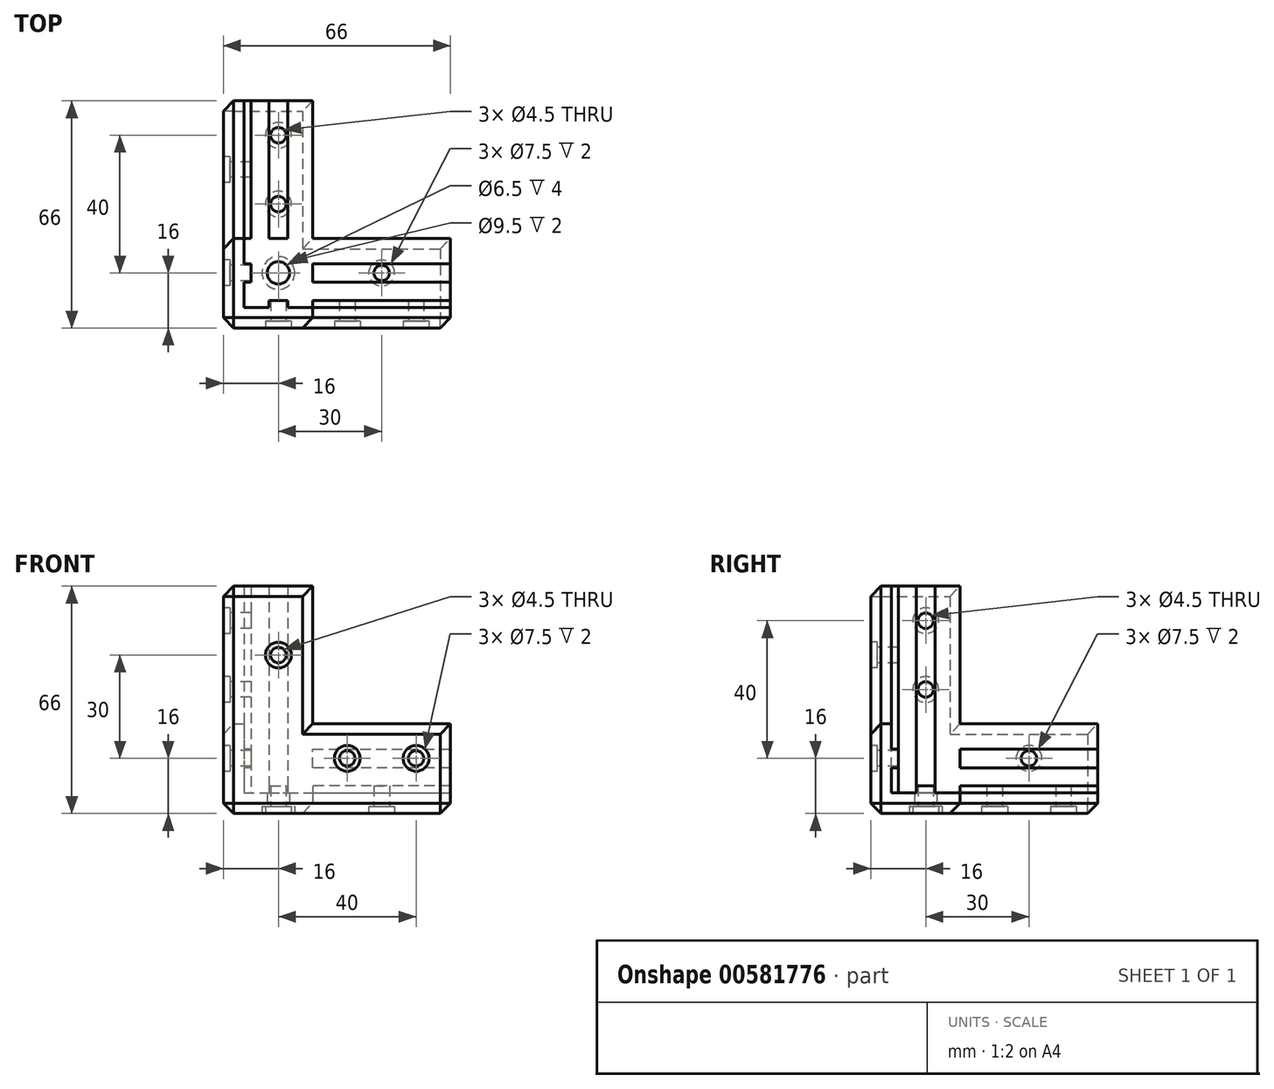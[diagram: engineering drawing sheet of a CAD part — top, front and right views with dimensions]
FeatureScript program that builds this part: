
annotation { "Feature Type Name" : "Feature", "Feature Type Description" : "" }
export const myFeature = defineFeature(function(context is Context, id is Id, definition is map)
    precondition{}
    {
        {
            var Q0;
            Q0=qCreatedBy(makeId("Top.planeOp"),FACE);
            var sketch = newSketch(context, id + "F0", { "sketchPlane" : qUnion([Q0])});
            skLineSegment(sketch, "E0", {"start": v(0, 0) * mm, "end": v(0, 66) * mm});
            skLineSegment(sketch, "E1", {"start": v(0, 66) * mm, "end": v(26, 66) * mm});
            skLineSegment(sketch, "E2", {"start": v(26, 66) * mm, "end": v(26, 26) * mm});
            skLineSegment(sketch, "E3", {"start": v(26, 26) * mm, "end": v(66, 26) * mm});
            skLineSegment(sketch, "E4", {"start": v(66, 26) * mm, "end": v(66, 0) * mm});
            skLineSegment(sketch, "E5", {"start": v(66, 0) * mm, "end": v(0, 0) * mm});
            skLineSegment(sketch, "E6", {"start": v(66, 6) * mm, "end": v(6, 6) * mm, "construction": true});
            skLineSegment(sketch, "E7", {"start": v(6, 6) * mm, "end": v(6, 66) * mm, "construction": true});
            skSolve(sketch);
        }
        {
            var Q0;
            Q0=qSketchRegion(id+"F0",true);
            extrude(context, id + "F1", {"entities" : qUnion([Q0]), "depth" : 6 * mm});
        }
        {
            var Q0;
            Q0=makeQuery(id+"F1.opExtrude","CAP_FACE",FACE,{"disambiguationData":[OSD([sQuery(id+"F0.wireOp",EDGE,"E0"),sQuery(id+"F0.wireOp",EDGE,"E1"),sQuery(id+"F0.wireOp",EDGE,"E2"),sQuery(id+"F0.wireOp",EDGE,"E3"),sQuery(id+"F0.wireOp",EDGE,"E4"),sQuery(id+"F0.wireOp",EDGE,"E5")])],"isStart":false});
            var sketch = newSketch(context, id + "F2", { "sketchPlane" : qUnion([Q0])});
            skLineSegment(sketch, "E8", {"start": v(0, 66) * mm, "end": v(6, 66) * mm});
            skLineSegment(sketch, "E9", {"start": v(6, 66) * mm, "end": v(6, 6) * mm});
            skLineSegment(sketch, "E10", {"start": v(6, 6) * mm, "end": v(66, 6) * mm});
            skLineSegment(sketch, "E11", {"start": v(66, 6) * mm, "end": v(66, 0) * mm});
            skLineSegment(sketch, "E12", {"start": v(66, 0) * mm, "end": v(0, 0) * mm});
            skLineSegment(sketch, "E13", {"start": v(0, 0) * mm, "end": v(0, 66) * mm});
            skSolve(sketch);
        }
        {
            var Q0;
            Q0=makeQuery(id+"F2.imprint","IMPRINT",FACE,{"disambiguationData":[TD([[makeQuery(id+"F2.imprint","IMPRINT",EDGE,{"derivedFrom":sQuery(id+"F2.wireOp",EDGE,"E8")}),-1.0]])]});
            extrude(context, id + "F3", {"entities" : qUnion([Q0]), "operationType" : NewBodyOperationType.ADD, "depth" : 20 * mm});
        }
        {
            var Q0;
            Q0=makeQuery(id+"F3.opExtrude","CAP_FACE",FACE,{"disambiguationData":[OSD([sQuery(id+"F2.wireOp",EDGE,"E8"),sQuery(id+"F2.wireOp",EDGE,"E9"),sQuery(id+"F2.wireOp",EDGE,"E10"),sQuery(id+"F2.wireOp",EDGE,"E11"),sQuery(id+"F2.wireOp",EDGE,"E12"),sQuery(id+"F2.wireOp",EDGE,"E13")])],"isStart":false});
            var sketch = newSketch(context, id + "F4", { "sketchPlane" : qUnion([Q0])});
            skLineSegment(sketch, "E14", {"start": v(6, 26) * mm, "end": v(0, 26) * mm});
            skLineSegment(sketch, "E15", {"start": v(0, 26) * mm, "end": v(0, 0) * mm});
            skLineSegment(sketch, "E16", {"start": v(0, 0) * mm, "end": v(26, 0) * mm});
            skLineSegment(sketch, "E17", {"start": v(26, 0) * mm, "end": v(26, 6) * mm});
            skLineSegment(sketch, "E18", {"start": v(26, 6) * mm, "end": v(6, 6) * mm});
            skLineSegment(sketch, "E19", {"start": v(6, 6) * mm, "end": v(6, 26) * mm});
            skSolve(sketch);
        }
        {
            var Q0;
            Q0=qSketchRegion(id+"F4",true);
            extrude(context, id + "F5", {"entities" : qUnion([Q0]), "operationType" : NewBodyOperationType.ADD, "depth" : 40 * mm});
        }
        {
            var Q0;
            Q0=makeQuery(id+"F1.opExtrude","CAP_FACE",FACE,{"disambiguationData":[OSD([sQuery(id+"F0.wireOp",EDGE,"E0"),sQuery(id+"F0.wireOp",EDGE,"E1"),sQuery(id+"F0.wireOp",EDGE,"E2"),sQuery(id+"F0.wireOp",EDGE,"E3"),sQuery(id+"F0.wireOp",EDGE,"E4"),sQuery(id+"F0.wireOp",EDGE,"E5")])],"isStart":false});
            var sketch = newSketch(context, id + "F6", { "sketchPlane" : qUnion([Q0])});
            skLineSegment(sketch, "E20", {"start": v(66, 16) * mm, "end": v(6, 16) * mm, "construction": true});
            skLineSegment(sketch, "E21", {"start": v(16, 66) * mm, "end": v(16, 6) * mm, "construction": true});
            skLineSegment(sketch, "E22", {"start": v(16, 6) * mm, "end": v(18.71, 6) * mm});
            skLineSegment(sketch, "E23", {"start": v(18.71, 6) * mm, "end": v(18.71, 8) * mm});
            skLineSegment(sketch, "E24", {"start": v(18.71, 8) * mm, "end": v(13.3, 8) * mm});
            skLineSegment(sketch, "E25", {"start": v(13.3, 8) * mm, "end": v(13.3, 6) * mm});
            skLineSegment(sketch, "E26", {"start": v(13.3, 6) * mm, "end": v(16, 6) * mm});
            skLineSegment(sketch, "E27", {"start": v(6, 16) * mm, "end": v(6, 18.7) * mm});
            skLineSegment(sketch, "E28", {"start": v(6, 18.7) * mm, "end": v(8, 18.7) * mm});
            skLineSegment(sketch, "E29", {"start": v(8, 18.7) * mm, "end": v(8, 13.29) * mm});
            skLineSegment(sketch, "E30", {"start": v(8, 13.29) * mm, "end": v(6, 13.29) * mm});
            skLineSegment(sketch, "E31", {"start": v(6, 13.29) * mm, "end": v(6, 16) * mm});
            skSolve(sketch);
        }
        {
            var Q0;
            Q0=qSketchRegion(id+"F6",true);
            extrude(context, id + "F7", {"entities" : qUnion([Q0]), "operationType" : NewBodyOperationType.ADD, "depth" : 60 * mm});
        }
        {
            var Q0;
            Q0=makeQuery(id+"F1.opExtrude","CAP_FACE",FACE,{"disambiguationData":[OSD([sQuery(id+"F0.wireOp",EDGE,"E0"),sQuery(id+"F0.wireOp",EDGE,"E1"),sQuery(id+"F0.wireOp",EDGE,"E2"),sQuery(id+"F0.wireOp",EDGE,"E3"),sQuery(id+"F0.wireOp",EDGE,"E4"),sQuery(id+"F0.wireOp",EDGE,"E5")])],"isStart":false});
            var sketch = newSketch(context, id + "F8", { "sketchPlane" : qUnion([Q0])});
            skLineSegment(sketch, "E32", {"start": v(66, 16) * mm, "end": v(8, 16) * mm, "construction": true});
            skLineSegment(sketch, "E33", {"start": v(66, 16) * mm, "end": v(66, 18.7) * mm});
            skLineSegment(sketch, "E34", {"start": v(66, 18.7) * mm, "end": v(26, 18.7) * mm});
            skLineSegment(sketch, "E35", {"start": v(26, 18.7) * mm, "end": v(26, 13.29) * mm});
            skLineSegment(sketch, "E36", {"start": v(26, 13.29) * mm, "end": v(66, 13.29) * mm});
            skLineSegment(sketch, "E37", {"start": v(66, 13.29) * mm, "end": v(66, 16) * mm});
            skLineSegment(sketch, "E38", {"start": v(16, 66) * mm, "end": v(16, 8) * mm, "construction": true});
            skLineSegment(sketch, "E39", {"start": v(16, 66) * mm, "end": v(13.3, 66) * mm});
            skLineSegment(sketch, "E40", {"start": v(13.3, 66) * mm, "end": v(13.3, 26) * mm});
            skLineSegment(sketch, "E41", {"start": v(13.3, 26) * mm, "end": v(18.7, 26) * mm});
            skLineSegment(sketch, "E42", {"start": v(18.7, 26) * mm, "end": v(18.7, 66) * mm});
            skLineSegment(sketch, "E43", {"start": v(18.7, 66) * mm, "end": v(16, 66) * mm});
            skSolve(sketch);
        }
        {
            var Q0;
            Q0=qSketchRegion(id+"F8",true);
            extrude(context, id + "F9", {"entities" : qUnion([Q0]), "operationType" : NewBodyOperationType.ADD, "depth" : 2 * mm});
        }
        {
            var Q0;
            {var subQ1=sQuery(id+"F2.wireOp",EDGE,"E10");var subQ2=sQuery(id+"F0.wireOp",EDGE,"E4");var subQ3=sQuery(id+"F4.wireOp",EDGE,"E18");Q0=makeQuery(id+"F7.boolean.opBoolean","SPLIT",FACE,{"disambiguationData":[TD([makeQuery(id+"F1.opExtrude","SWEPT_FACE",FACE,{"disambiguationData":[OSD([subQ2])]})])],"derivedFrom":makeQuery(id+"F5.boolean.opBoolean","MERGE",FACE,{"derivedFrom":[makeQuery(id+"F3.opExtrude","SWEPT_FACE",FACE,{"disambiguationData":[OSD([subQ1])]}),makeQuery(id+"F5.opExtrude","SWEPT_FACE",FACE,{"disambiguationData":[OSD([subQ3])]})]})});}
            var sketch = newSketch(context, id + "F10", { "sketchPlane" : qUnion([Q0])});
            skLineSegment(sketch, "E44", {"start": v(-66, 16) * mm, "end": v(-26, 16) * mm, "construction": true});
            skLineSegment(sketch, "E45", {"start": v(-66, 16) * mm, "end": v(-66, 13.3) * mm});
            skLineSegment(sketch, "E46", {"start": v(-66, 13.3) * mm, "end": v(-26, 13.3) * mm});
            skLineSegment(sketch, "E47", {"start": v(-26, 13.3) * mm, "end": v(-26, 16) * mm});
            skLineSegment(sketch, "E48", {"start": v(-26, 18.71) * mm, "end": v(-66, 18.71) * mm});
            skLineSegment(sketch, "E49", {"start": v(-66, 18.71) * mm, "end": v(-66, 16) * mm});
            skLineSegment(sketch, "E50", {"start": v(-26, 18.71) * mm, "end": v(-26, 16) * mm});
            skSolve(sketch);
        }
        {
            var Q0;
            Q0=qSketchRegion(id+"F10",true);
            extrude(context, id + "F11", {"entities" : qUnion([Q0]), "operationType" : NewBodyOperationType.ADD, "depth" : 2 * mm});
        }
        {
            var Q0;
            {var subQ0=sQuery(id+"F2.wireOp",EDGE,"E9");var subQ3=sQuery(id+"F0.wireOp",EDGE,"E1");var subQ5=sQuery(id+"F4.wireOp",EDGE,"E19");Q0=makeQuery(id+"F7.boolean.opBoolean","SPLIT",FACE,{"disambiguationData":[TD([makeQuery(id+"F1.opExtrude","SWEPT_FACE",FACE,{"disambiguationData":[OSD([subQ3])]})])],"derivedFrom":makeQuery(id+"F5.boolean.opBoolean","MERGE",FACE,{"derivedFrom":[makeQuery(id+"F3.opExtrude","SWEPT_FACE",FACE,{"disambiguationData":[OSD([subQ0])]}),makeQuery(id+"F5.opExtrude","SWEPT_FACE",FACE,{"disambiguationData":[OSD([subQ5])]})]})});}
            var sketch = newSketch(context, id + "F12", { "sketchPlane" : qUnion([Q0])});
            skLineSegment(sketch, "E51", {"start": v(66, 16) * mm, "end": v(26, 16) * mm, "construction": true});
            skLineSegment(sketch, "E52", {"start": v(66, 16) * mm, "end": v(66, 18.71) * mm});
            skLineSegment(sketch, "E53", {"start": v(66, 18.71) * mm, "end": v(26, 18.7) * mm});
            skLineSegment(sketch, "E54", {"start": v(26, 18.7) * mm, "end": v(26, 13.29) * mm});
            skLineSegment(sketch, "E55", {"start": v(26, 13.29) * mm, "end": v(66, 13.29) * mm});
            skLineSegment(sketch, "E56", {"start": v(66, 16) * mm, "end": v(66, 13.29) * mm});
            skSolve(sketch);
        }
        {
            var Q0;
            Q0=qSketchRegion(id+"F12",true);
            extrude(context, id + "F13", {"entities" : qUnion([Q0]), "operationType" : NewBodyOperationType.ADD, "depth" : 2 * mm});
        }
        {
            var Q0;
            Q0=makeQuery(id+"F5.boolean.opBoolean","MERGE",FACE,{"derivedFrom":[makeQuery(id+"F3.boolean.opBoolean","MERGE",FACE,{"derivedFrom":[makeQuery(id+"F1.opExtrude","SWEPT_FACE",FACE,{"disambiguationData":[OSD([sQuery(id+"F0.wireOp",EDGE,"E5")])]}),makeQuery(id+"F3.opExtrude","SWEPT_FACE",FACE,{"disambiguationData":[OSD([sQuery(id+"F2.wireOp",EDGE,"E12")])]})]}),makeQuery(id+"F5.opExtrude","SWEPT_FACE",FACE,{"disambiguationData":[OSD([sQuery(id+"F4.wireOp",EDGE,"E16")])]})]});
            var sketch = newSketch(context, id + "F14", { "sketchPlane" : qUnion([Q0])});
            skLineSegment(sketch, "E57", {"start": v(6, 66) * mm, "end": v(6, 6) * mm, "construction": true});
            skLineSegment(sketch, "E58", {"start": v(6, 6) * mm, "end": v(66, 6) * mm, "construction": true});
            skCircle(sketch, "E59", {"center": v(56, 16) * mm, "radius": 2.25 * mm});
            skCircle(sketch, "E60", {"center": v(36, 16) * mm, "radius": 2.25 * mm});
            skCircle(sketch, "E61", {"center": v(16, 46) * mm, "radius": 2.25 * mm});
            skLineSegment(sketch, "E62", {"start": v(26, 26) * mm, "end": v(6, 26) * mm, "construction": true});
            skLineSegment(sketch, "E63", {"start": v(26, 26) * mm, "end": v(26, 6) * mm, "construction": true});
            skSolve(sketch);
        }
        {
            var Q0;
            Q0=makeQuery(id+"F14.imprint","IMPRINT",FACE,{"disambiguationData":[TD([[makeQuery(id+"F14.imprint","IMPRINT",EDGE,{"derivedFrom":sQuery(id+"F14.wireOp",EDGE,"E59")}),1.0]])]});
            var Q1;
            Q1=makeQuery(id+"F14.imprint","IMPRINT",FACE,{"disambiguationData":[TD([[makeQuery(id+"F14.imprint","IMPRINT",EDGE,{"derivedFrom":sQuery(id+"F14.wireOp",EDGE,"E61")}),1.0]])]});
            var Q2;
            Q2=makeQuery(id+"F14.imprint","IMPRINT",FACE,{"disambiguationData":[TD([[makeQuery(id+"F14.imprint","IMPRINT",EDGE,{"derivedFrom":sQuery(id+"F14.wireOp",EDGE,"E60")}),1.0]])]});
            extrude(context, id + "F15", {"entities" : qUnion([Q0, Q1, Q2]), "operationType" : NewBodyOperationType.REMOVE, "endBound" : BoundingType.UP_TO_NEXT, "oppositeDirection" : true, "depth" : 25 * mm});
        }
        {
            var Q0;
            Q0=makeQuery(id+"F5.boolean.opBoolean","MERGE",FACE,{"derivedFrom":[makeQuery(id+"F3.boolean.opBoolean","MERGE",FACE,{"derivedFrom":[makeQuery(id+"F1.opExtrude","SWEPT_FACE",FACE,{"disambiguationData":[OSD([sQuery(id+"F0.wireOp",EDGE,"E0")])]}),makeQuery(id+"F3.opExtrude","SWEPT_FACE",FACE,{"disambiguationData":[OSD([sQuery(id+"F2.wireOp",EDGE,"E13")])]})]}),makeQuery(id+"F5.opExtrude","SWEPT_FACE",FACE,{"disambiguationData":[OSD([sQuery(id+"F4.wireOp",EDGE,"E15")])]})]});
            var sketch = newSketch(context, id + "F16", { "sketchPlane" : qUnion([Q0])});
            skLineSegment(sketch, "E64", {"start": v(-6, 66) * mm, "end": v(-6, 6) * mm, "construction": true});
            skLineSegment(sketch, "E65", {"start": v(-6, 6) * mm, "end": v(-66, 6) * mm, "construction": true});
            skCircle(sketch, "E66", {"center": v(-16, 56) * mm, "radius": 2.25 * mm});
            skCircle(sketch, "E67", {"center": v(-46, 16) * mm, "radius": 2.25 * mm});
            skCircle(sketch, "E68", {"center": v(-16, 36) * mm, "radius": 2.25 * mm});
            skSolve(sketch);
        }
        {
            var Q0;
            Q0=qSketchRegion(id+"F16",true);
            extrude(context, id + "F17", {"entities" : qUnion([Q0]), "operationType" : NewBodyOperationType.REMOVE, "endBound" : BoundingType.UP_TO_NEXT, "oppositeDirection" : true, "depth" : 25 * mm});
        }
        {
            var Q0;
            Q0=makeQuery(id+"F1.opExtrude","CAP_FACE",FACE,{"disambiguationData":[OSD([sQuery(id+"F0.wireOp",EDGE,"E0"),sQuery(id+"F0.wireOp",EDGE,"E1"),sQuery(id+"F0.wireOp",EDGE,"E2"),sQuery(id+"F0.wireOp",EDGE,"E3"),sQuery(id+"F0.wireOp",EDGE,"E4"),sQuery(id+"F0.wireOp",EDGE,"E5")])],"isStart":true});
            var sketch = newSketch(context, id + "F18", { "sketchPlane" : qUnion([Q0])});
            skLineSegment(sketch, "E69", {"start": v(66, -6) * mm, "end": v(6, -6) * mm, "construction": true});
            skLineSegment(sketch, "E70", {"start": v(6, -6) * mm, "end": v(6, -66) * mm, "construction": true});
            skCircle(sketch, "E71", {"center": v(16, -16) * mm, "radius": 3.25 * mm});
            skCircle(sketch, "E72", {"center": v(46, -16) * mm, "radius": 2.25 * mm});
            skCircle(sketch, "E73", {"center": v(16, -56) * mm, "radius": 2.25 * mm});
            skCircle(sketch, "E74", {"center": v(16, -36) * mm, "radius": 2.25 * mm});
            skSolve(sketch);
        }
        {
            var Q0;
            Q0=qSketchRegion(id+"F18",true);
            extrude(context, id + "F19", {"entities" : qUnion([Q0]), "operationType" : NewBodyOperationType.REMOVE, "endBound" : BoundingType.UP_TO_NEXT, "oppositeDirection" : true, "depth" : 25 * mm});
        }
        {
            var Q0;
            Q0=makeQuery(id+"F5.boolean.opBoolean","MERGE",FACE,{"derivedFrom":[makeQuery(id+"F3.boolean.opBoolean","MERGE",FACE,{"derivedFrom":[makeQuery(id+"F1.opExtrude","SWEPT_FACE",FACE,{"disambiguationData":[OSD([sQuery(id+"F0.wireOp",EDGE,"E5")])]}),makeQuery(id+"F3.opExtrude","SWEPT_FACE",FACE,{"disambiguationData":[OSD([sQuery(id+"F2.wireOp",EDGE,"E12")])]})]}),makeQuery(id+"F5.opExtrude","SWEPT_FACE",FACE,{"disambiguationData":[OSD([sQuery(id+"F4.wireOp",EDGE,"E16")])]})]});
            var sketch = newSketch(context, id + "F20", { "sketchPlane" : qUnion([Q0])});
            skCircle(sketch, "E75", {"center": v(16, 46) * mm, "radius": 3.75 * mm});
            skCircle(sketch, "E76", {"center": v(36, 16) * mm, "radius": 3.75 * mm});
            skCircle(sketch, "E77", {"center": v(56, 16) * mm, "radius": 3.75 * mm});
            skSolve(sketch);
        }
        {
            var Q0;
            Q0=qSketchRegion(id+"F20",true);
            extrude(context, id + "F21", {"entities" : qUnion([Q0]), "operationType" : NewBodyOperationType.REMOVE, "oppositeDirection" : true, "depth" : 2 * mm});
        }
        {
            var Q0;
            Q0=makeQuery(id+"F5.boolean.opBoolean","MERGE",FACE,{"derivedFrom":[makeQuery(id+"F3.boolean.opBoolean","MERGE",FACE,{"derivedFrom":[makeQuery(id+"F1.opExtrude","SWEPT_FACE",FACE,{"disambiguationData":[OSD([sQuery(id+"F0.wireOp",EDGE,"E0")])]}),makeQuery(id+"F3.opExtrude","SWEPT_FACE",FACE,{"disambiguationData":[OSD([sQuery(id+"F2.wireOp",EDGE,"E13")])]})]}),makeQuery(id+"F5.opExtrude","SWEPT_FACE",FACE,{"disambiguationData":[OSD([sQuery(id+"F4.wireOp",EDGE,"E15")])]})]});
            var sketch = newSketch(context, id + "F22", { "sketchPlane" : qUnion([Q0])});
            skCircle(sketch, "E78", {"center": v(-16, 56) * mm, "radius": 3.75 * mm});
            skCircle(sketch, "E79", {"center": v(-46, 16) * mm, "radius": 3.75 * mm});
            skCircle(sketch, "E80", {"center": v(-16, 36) * mm, "radius": 3.75 * mm});
            skSolve(sketch);
        }
        {
            var Q0;
            Q0=qSketchRegion(id+"F22",true);
            extrude(context, id + "F23", {"entities" : qUnion([Q0]), "operationType" : NewBodyOperationType.REMOVE, "oppositeDirection" : true, "depth" : 2 * mm});
        }
        {
            var Q0;
            Q0=makeQuery(id+"F1.opExtrude","CAP_FACE",FACE,{"disambiguationData":[OSD([sQuery(id+"F0.wireOp",EDGE,"E0"),sQuery(id+"F0.wireOp",EDGE,"E1"),sQuery(id+"F0.wireOp",EDGE,"E2"),sQuery(id+"F0.wireOp",EDGE,"E3"),sQuery(id+"F0.wireOp",EDGE,"E4"),sQuery(id+"F0.wireOp",EDGE,"E5")])],"isStart":true});
            var sketch = newSketch(context, id + "F24", { "sketchPlane" : qUnion([Q0])});
            skCircle(sketch, "E81", {"center": v(16, -56) * mm, "radius": 3.75 * mm});
            skCircle(sketch, "E82", {"center": v(16, -16) * mm, "radius": 4.75 * mm});
            skCircle(sketch, "E83", {"center": v(46, -16) * mm, "radius": 3.75 * mm});
            skCircle(sketch, "E84", {"center": v(16, -36) * mm, "radius": 3.75 * mm});
            skSolve(sketch);
        }
        {
            var Q0;
            Q0=qSketchRegion(id+"F24",true);
            extrude(context, id + "F25", {"entities" : qUnion([Q0]), "operationType" : NewBodyOperationType.REMOVE, "oppositeDirection" : true, "depth" : 2 * mm});
        }
        {
            var Q0;
            Q0=makeQuery(id+"F1.opExtrude","CAP_EDGE",EDGE,{"disambiguationData":[OSD([sQuery(id+"F0.wireOp",EDGE,"E5")])],"isStart":true});
            var Q1;
            Q1=makeQuery(id+"F1.opExtrude","CAP_EDGE",EDGE,{"disambiguationData":[OSD([sQuery(id+"F0.wireOp",EDGE,"E0")])],"isStart":true});
            var Q2;
            Q2=makeQuery(id+"F5.boolean.opBoolean","MERGE",EDGE,{"derivedFrom":[makeQuery(id+"F3.boolean.opBoolean","MERGE",EDGE,{"derivedFrom":[makeQuery(id+"F1.opExtrude","SWEPT_EDGE",EDGE,{"disambiguationData":[OSD([sQuery(id+"F0.wireOp",EDGE,"E0"),sQuery(id+"F0.wireOp",EDGE,"E5")])]}),makeQuery(id+"F3.opExtrude","SWEPT_EDGE",EDGE,{"disambiguationData":[OSD([sQuery(id+"F2.wireOp",EDGE,"E12"),sQuery(id+"F2.wireOp",EDGE,"E13")])]})]}),makeQuery(id+"F5.opExtrude","SWEPT_EDGE",EDGE,{"disambiguationData":[OSD([sQuery(id+"F4.wireOp",EDGE,"E15"),sQuery(id+"F4.wireOp",EDGE,"E16")])]})]});
            var Q3;
            Q3=makeQuery(id+"F5.opExtrude","SWEPT_EDGE",EDGE,{"disambiguationData":[OSD([sQuery(id+"F2.wireOp",EDGE,"E13"),sQuery(id+"F4.wireOp",EDGE,"E14"),sQuery(id+"F4.wireOp",EDGE,"E15")])]});
            var Q4;
            Q4=makeQuery(id+"F3.opExtrude","CAP_EDGE",EDGE,{"disambiguationData":[OSD([sQuery(id+"F2.wireOp",EDGE,"E13")])],"isStart":false});
            var Q5;
            Q5=makeQuery(id+"F5.opExtrude","SWEPT_EDGE",EDGE,{"disambiguationData":[OSD([sQuery(id+"F2.wireOp",EDGE,"E12"),sQuery(id+"F4.wireOp",EDGE,"E16"),sQuery(id+"F4.wireOp",EDGE,"E17")])]});
            var Q6;
            Q6=makeQuery(id+"F3.opExtrude","CAP_EDGE",EDGE,{"disambiguationData":[OSD([sQuery(id+"F2.wireOp",EDGE,"E12")])],"isStart":false});
            var Q7;
            Q7=makeQuery(id+"F5.opExtrude","CAP_EDGE",EDGE,{"disambiguationData":[OSD([sQuery(id+"F4.wireOp",EDGE,"E15")])],"isStart":false});
            var Q8;
            Q8=makeQuery(id+"F5.opExtrude","CAP_EDGE",EDGE,{"disambiguationData":[OSD([sQuery(id+"F4.wireOp",EDGE,"E16")])],"isStart":false});
            var Q9;
            Q9=makeQuery(id+"F3.boolean.opBoolean","MERGE",EDGE,{"derivedFrom":[makeQuery(id+"F1.opExtrude","SWEPT_EDGE",EDGE,{"disambiguationData":[OSD([sQuery(id+"F0.wireOp",EDGE,"E0"),sQuery(id+"F0.wireOp",EDGE,"E1")])]}),makeQuery(id+"F3.opExtrude","SWEPT_EDGE",EDGE,{"disambiguationData":[OSD([sQuery(id+"F2.wireOp",EDGE,"E8"),sQuery(id+"F2.wireOp",EDGE,"E13")])]})]});
            var Q10;
            Q10=makeQuery(id+"F1.opExtrude","CAP_EDGE",EDGE,{"disambiguationData":[OSD([sQuery(id+"F0.wireOp",EDGE,"E1")])],"isStart":true});
            var Q11;
            Q11=makeQuery(id+"F3.boolean.opBoolean","MERGE",EDGE,{"derivedFrom":[makeQuery(id+"F1.opExtrude","SWEPT_EDGE",EDGE,{"disambiguationData":[OSD([sQuery(id+"F0.wireOp",EDGE,"E4"),sQuery(id+"F0.wireOp",EDGE,"E5")])]}),makeQuery(id+"F3.opExtrude","SWEPT_EDGE",EDGE,{"disambiguationData":[OSD([sQuery(id+"F2.wireOp",EDGE,"E11"),sQuery(id+"F2.wireOp",EDGE,"E12")])]})]});
            var Q12;
            Q12=makeQuery(id+"F1.opExtrude","CAP_EDGE",EDGE,{"disambiguationData":[OSD([sQuery(id+"F0.wireOp",EDGE,"E4")])],"isStart":true});
            var Q13;
            Q13=makeQuery(id+"F1.opExtrude","CAP_EDGE",EDGE,{"disambiguationData":[OSD([sQuery(id+"F0.wireOp",EDGE,"E3")])],"isStart":true});
            var Q14;
            Q14=makeQuery(id+"F1.opExtrude","CAP_EDGE",EDGE,{"disambiguationData":[OSD([sQuery(id+"F0.wireOp",EDGE,"E2")])],"isStart":true});
            chamfer(context, id + "F26", {"entities" : qUnion([Q0, Q1, Q2, Q3, Q4, Q5, Q6, Q7, Q8, Q9, Q10, Q11, Q12, Q13, Q14]), "width" : 3 * mm, "tangentPropagation" : true});
        }
    });
